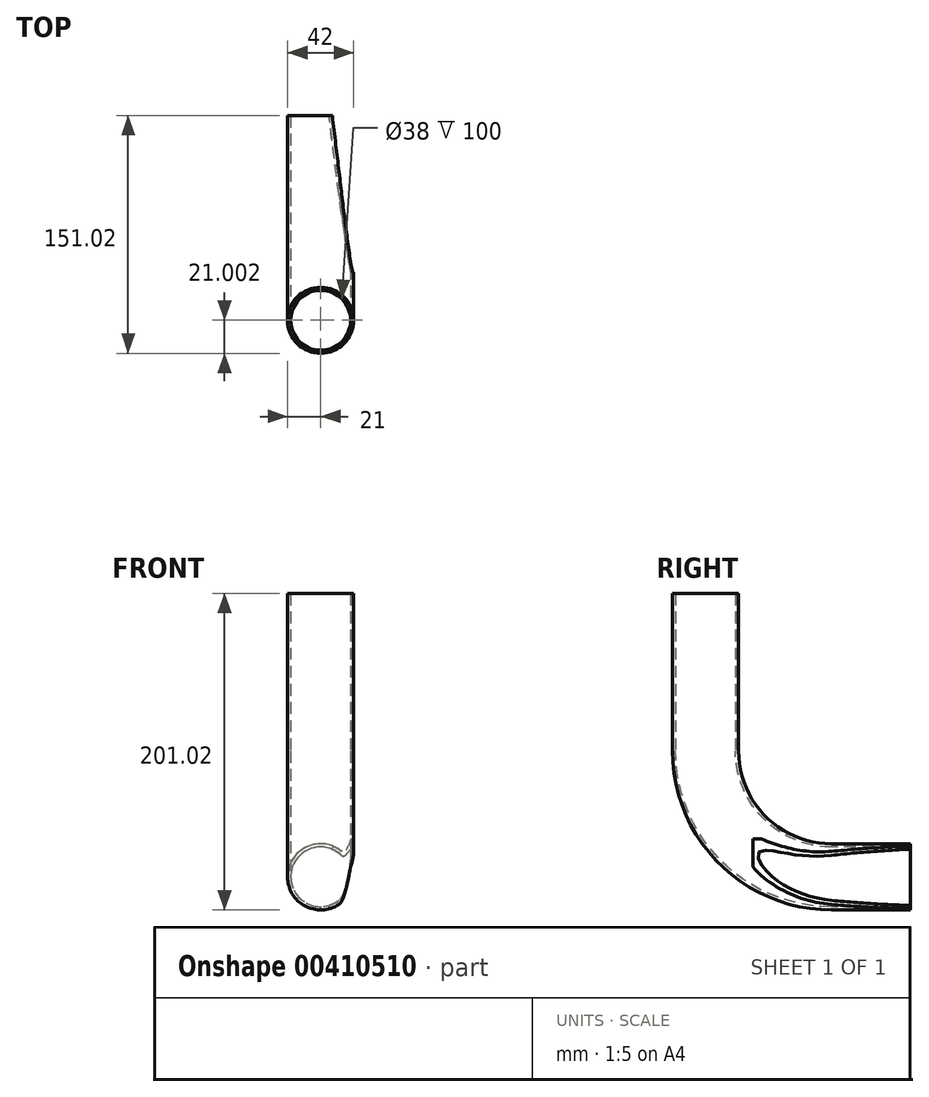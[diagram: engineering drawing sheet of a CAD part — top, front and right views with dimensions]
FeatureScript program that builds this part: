
annotation { "Feature Type Name" : "Feature", "Feature Type Description" : "" }
export const myFeature = defineFeature(function(context is Context, id is Id, definition is map)
    precondition{}
    {
        {
            var Q0;
            Q0=qCreatedBy(makeId("Right.planeOp"),FACE);
            var sketch = newSketch(context, id + "F0", { "sketchPlane" : qUnion([Q0])});
            skArc(sketch, "E0", {"start": v(0, -80) * mm, "mid": v(-56.57, -56.57) * mm, "end": v(-80, 0) * mm});
            skSolve(sketch);
        }
        {
            var Q0;
            Q0=qCreatedBy(makeId("Top.planeOp"),FACE);
            var sketch = newSketch(context, id + "F1", { "sketchPlane" : qUnion([Q0])});
            skCircle(sketch, "E1", {"center": v(0, -80.02) * mm, "radius": 21 * mm});
            skCircle(sketch, "E2", {"center": v(0, -80.02) * mm, "radius": 19 * mm});
            skSolve(sketch);
        }
        {
            var Q0;
            Q0=makeQuery(id+"F1.imprint","IMPRINT",FACE,{"disambiguationData":[TD([[makeQuery(id+"F1.imprint","IMPRINT",EDGE,{"derivedFrom":sQuery(id+"F1.wireOp",EDGE,"E1")}),1.0]])]});
            var Q1;
            Q1=sQuery(id+"F0.wireOp",EDGE,"E0");
            sweep(context, id + "F2", {"profiles" : qUnion([Q0]), "path" : qUnion([Q1])});
        }
        {
            var Q0;
            Q0=makeQuery(id+"F2.opSweep","CAP_FACE",FACE,{"disambiguationData":[OSD([sQuery(id+"F0.wireOp",VERTEX,"E0.end"),sQuery(id+"F1.wireOp",EDGE,"E1"),sQuery(id+"F1.wireOp",EDGE,"E2")])],"isStart":true});
            extrude(context, id + "F3", {"entities" : qUnion([Q0]), "operationType" : NewBodyOperationType.ADD, "depth" : 100 * mm});
        }
        {
            var Q0;
            Q0=makeQuery(id+"F2.opSweep","CAP_FACE",FACE,{"disambiguationData":[OSD([sQuery(id+"F0.wireOp",VERTEX,"E0.start"),sQuery(id+"F1.wireOp",EDGE,"E1"),sQuery(id+"F1.wireOp",EDGE,"E2")])],"isStart":false});
            extrude(context, id + "F4", {"entities" : qUnion([Q0]), "operationType" : NewBodyOperationType.ADD, "depth" : 50 * mm});
        }
        {
            var Q0;
            Q0=makeQuery(id+"F4.opExtrude","SWEPT_FACE",FACE,{"disambiguationData":[OSD([sQuery(id+"F0.wireOp",VERTEX,"E0.start"),sQuery(id+"F1.wireOp",EDGE,"E2")])]});
            cPlane(context, id + "F5", {"entities" : qUnion([Q0]), "cplaneType" : CPlaneType.LINE_ANGLE, "offset" : 25 * mm, "angle" : 3 * degree, "width" : 150 * mm, "height" : 150 * mm});
        }
        {
            var Q0;
            Q0=qCreatedBy(id+"F5.planeOp",FACE);
            var sketch = newSketch(context, id + "F6", { "sketchPlane" : qUnion([Q0])});
            skLineSegment(sketch, "E3", {"start": v(-2.15, 50) * mm, "end": v(-14.42, -50) * mm, "construction": true});
            skLineSegment(sketch, "E4", {"start": v(-14.42, -50) * mm, "end": v(-50, -50) * mm, "construction": true});
            skLineSegment(sketch, "E5", {"start": v(-50, -50) * mm, "end": v(-50, 50) * mm, "construction": true});
            skLineSegment(sketch, "E6", {"start": v(-50, 50) * mm, "end": v(-2.15, 50) * mm, "construction": true});
            skLineSegment(sketch, "E7.0", {"start": v(23.19, 50) * mm, "end": v(-14.81, 50) * mm});
            skLineSegment(sketch, "E8.MirrorCS", {"start": v(58.38, 50) * mm, "end": v(10.52, 50) * mm});
            skLineSegment(sketch, "E9.MirrorCS", {"start": v(58.38, -50) * mm, "end": v(58.38, 50) * mm});
            skLineSegment(sketch, "E10.MirrorCS", {"start": v(10.52, 50) * mm, "end": v(22.8, -50) * mm});
            skLineSegment(sketch, "E11.MirrorCS", {"start": v(22.8, -50) * mm, "end": v(58.38, -50) * mm});
            skSolve(sketch);
        }
        {
            var Q0;
            Q0=qSketchRegion(id+"F6",true);
            extrude(context, id + "F7", {"entities" : qUnion([Q0]), "operationType" : NewBodyOperationType.REMOVE, "depth" : 50 * mm, "symmetric" : true});
        }
    });
